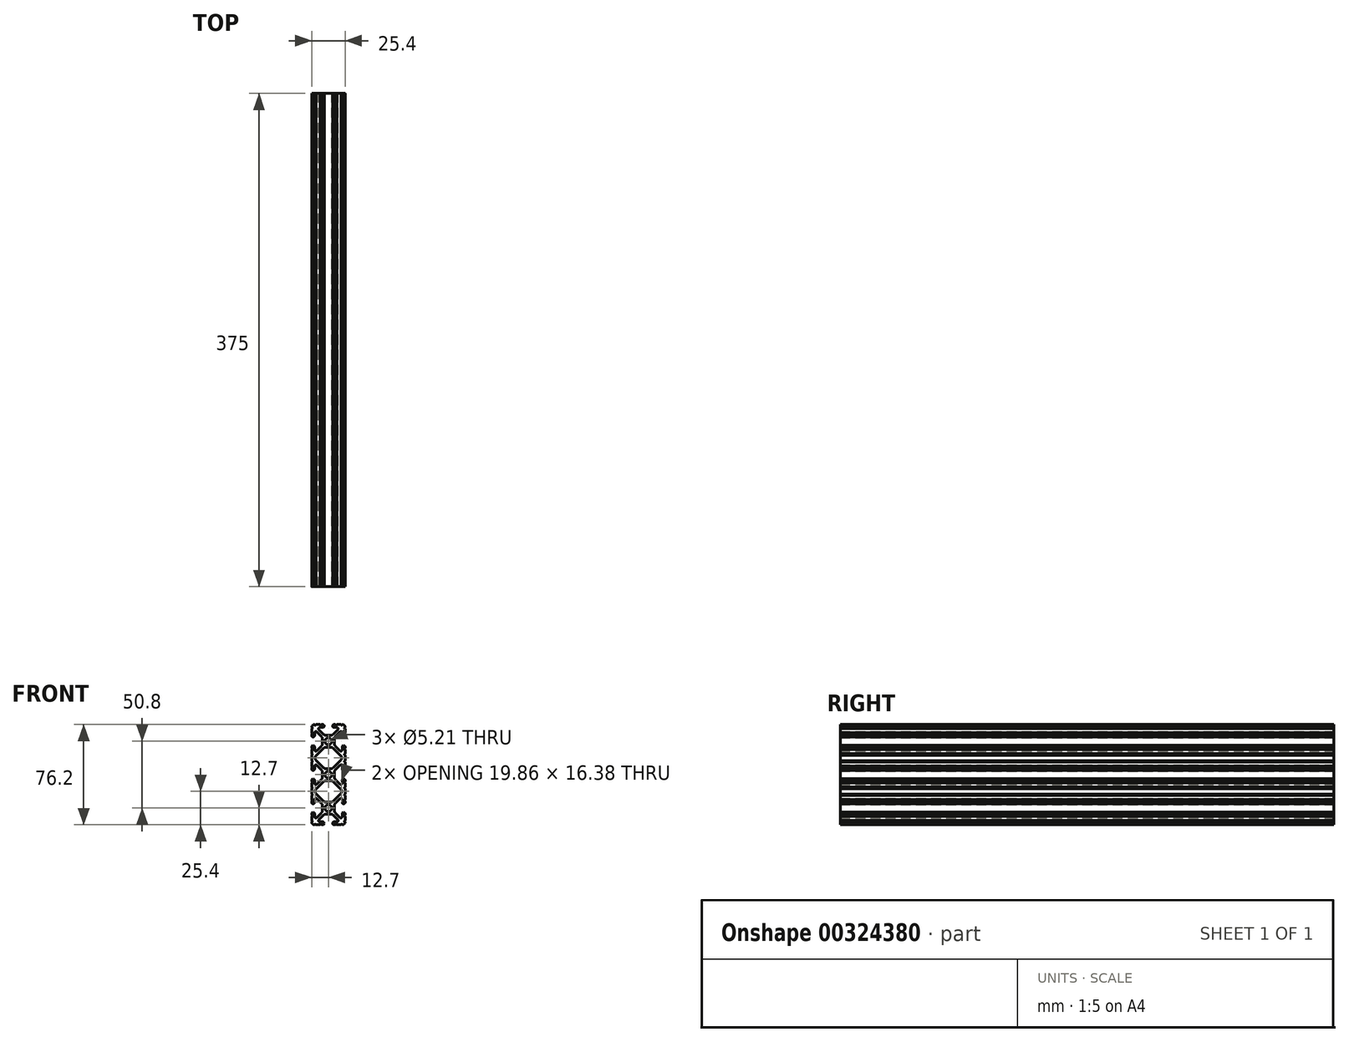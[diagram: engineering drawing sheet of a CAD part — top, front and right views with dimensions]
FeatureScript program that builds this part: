
annotation { "Feature Type Name" : "Feature", "Feature Type Description" : "" }
export const myFeature = defineFeature(function(context is Context, id is Id, definition is map)
    precondition{}
    {
        {
            var Q0;
            Q0=qCreatedBy(makeId("Front.planeOp"),FACE);
            var sketch = newSketch(context, id + "F0", { "sketchPlane" : qUnion([Q0])});
            skArc(sketch, "E0", {"start": v(2.6, 25.4) * mm, "mid": v(0, 28) * mm, "end": v(-2.6, 25.4) * mm});
            skArc(sketch, "E1", {"start": v(-2.6, 25.4) * mm, "mid": v(0, 22.8) * mm, "end": v(2.6, 25.4) * mm});
            skArc(sketch, "E2", {"start": v(-10.57, 38.1) * mm, "mid": v(-10.06, 37.6) * mm, "end": v(-9.55, 38.1) * mm});
            skArc(sketch, "E3", {"start": v(-10.57, 38.1) * mm, "mid": v(-12.08, 37.48) * mm, "end": v(-12.7, 35.97) * mm});
            skArc(sketch, "E4", {"start": v(-12.7, 34.95) * mm, "mid": v(-12.2, 35.46) * mm, "end": v(-12.7, 35.97) * mm});
            skLineSegment(sketch, "E5", {"start": v(-12.7, 34.95) * mm, "end": v(-12.7, 31.72) * mm});
            skArc(sketch, "E6", {"start": v(-12.7, 30.7) * mm, "mid": v(-12.2, 31.22) * mm, "end": v(-12.7, 31.72) * mm});
            skLineSegment(sketch, "E7", {"start": v(-12.7, 30.7) * mm, "end": v(-12.7, 29.7) * mm});
            skArc(sketch, "E8", {"start": v(-12.7, 29.7) * mm, "mid": v(-11.6, 28.6) * mm, "end": v(-10.5, 29.7) * mm});
            skLineSegment(sketch, "E9", {"start": v(-10.5, 29.7) * mm, "end": v(-10.5, 31.87) * mm});
            skArc(sketch, "E10", {"start": v(-8.76, 32.6) * mm, "mid": v(-9.86, 32.81) * mm, "end": v(-10.5, 31.87) * mm});
            skLineSegment(sketch, "E11", {"start": v(-8.76, 32.6) * mm, "end": v(-5.44, 29.28) * mm});
            skArc(sketch, "E12", {"start": v(-4.5, 27.03) * mm, "mid": v(-4.75, 28.25) * mm, "end": v(-5.44, 29.28) * mm});
            skLineSegment(sketch, "E13", {"start": v(-4.5, 27.03) * mm, "end": v(-4.5, 23.77) * mm});
            skArc(sketch, "E14", {"start": v(-5.44, 21.52) * mm, "mid": v(-4.75, 22.55) * mm, "end": v(-4.5, 23.77) * mm});
            skLineSegment(sketch, "E15", {"start": v(-5.44, 21.52) * mm, "end": v(-8.76, 18.2) * mm});
            skArc(sketch, "E16", {"start": v(-10.5, 18.93) * mm, "mid": v(-9.86, 17.99) * mm, "end": v(-8.76, 18.2) * mm});
            skLineSegment(sketch, "E17", {"start": v(-10.5, 18.93) * mm, "end": v(-10.5, 21.1) * mm});
            skArc(sketch, "E18", {"start": v(-10.5, 21.1) * mm, "mid": v(-11.6, 22.2) * mm, "end": v(-12.7, 21.1) * mm});
            skLineSegment(sketch, "E19", {"start": v(-12.7, 21.1) * mm, "end": v(-12.7, 20.1) * mm});
            skArc(sketch, "E20", {"start": v(-12.7, 19.08) * mm, "mid": v(-12.2, 19.58) * mm, "end": v(-12.7, 20.1) * mm});
            skLineSegment(sketch, "E21", {"start": v(-12.7, 19.08) * mm, "end": v(-12.7, 15.85) * mm});
            skArc(sketch, "E22", {"start": v(-12.7, 14.83) * mm, "mid": v(-12.2, 15.34) * mm, "end": v(-12.7, 15.85) * mm});
            skLineSegment(sketch, "E23", {"start": v(-12.7, 14.83) * mm, "end": v(-12.7, 10.57) * mm});
            skArc(sketch, "E24", {"start": v(-12.7, 9.55) * mm, "mid": v(-12.2, 10.06) * mm, "end": v(-12.7, 10.57) * mm});
            skLineSegment(sketch, "E25", {"start": v(-12.7, 9.55) * mm, "end": v(-12.7, 6.32) * mm});
            skArc(sketch, "E26", {"start": v(-12.7, 5.3) * mm, "mid": v(-12.2, 5.82) * mm, "end": v(-12.7, 6.32) * mm});
            skLineSegment(sketch, "E27", {"start": v(-12.7, 5.3) * mm, "end": v(-12.7, 4.3) * mm});
            skArc(sketch, "E28", {"start": v(-12.7, 4.3) * mm, "mid": v(-11.6, 3.2) * mm, "end": v(-10.5, 4.3) * mm});
            skLineSegment(sketch, "E29", {"start": v(-10.5, 4.3) * mm, "end": v(-10.5, 6.47) * mm});
            skArc(sketch, "E30", {"start": v(-8.76, 7.2) * mm, "mid": v(-9.86, 7.41) * mm, "end": v(-10.5, 6.47) * mm});
            skLineSegment(sketch, "E31", {"start": v(-8.76, 7.2) * mm, "end": v(-5.44, 3.88) * mm});
            skArc(sketch, "E32", {"start": v(-4.5, 1.63) * mm, "mid": v(-4.75, 2.85) * mm, "end": v(-5.44, 3.88) * mm});
            skLineSegment(sketch, "E33", {"start": v(-4.5, 1.63) * mm, "end": v(-4.5, -1.63) * mm});
            skArc(sketch, "E34", {"start": v(-5.44, -3.88) * mm, "mid": v(-4.75, -2.85) * mm, "end": v(-4.5, -1.63) * mm});
            skLineSegment(sketch, "E35", {"start": v(-5.44, -3.88) * mm, "end": v(-8.76, -7.2) * mm});
            skArc(sketch, "E36", {"start": v(-10.5, -6.47) * mm, "mid": v(-9.86, -7.41) * mm, "end": v(-8.76, -7.2) * mm});
            skLineSegment(sketch, "E37", {"start": v(-10.5, -6.47) * mm, "end": v(-10.5, -4.3) * mm});
            skArc(sketch, "E38", {"start": v(-10.5, -4.3) * mm, "mid": v(-11.6, -3.2) * mm, "end": v(-12.7, -4.3) * mm});
            skLineSegment(sketch, "E39", {"start": v(-12.7, -4.3) * mm, "end": v(-12.7, -5.3) * mm});
            skArc(sketch, "E40", {"start": v(-12.7, -6.32) * mm, "mid": v(-12.2, -5.82) * mm, "end": v(-12.7, -5.3) * mm});
            skLineSegment(sketch, "E41", {"start": v(-12.7, -6.32) * mm, "end": v(-12.7, -9.55) * mm});
            skArc(sketch, "E42", {"start": v(-12.7, -10.57) * mm, "mid": v(-12.2, -10.06) * mm, "end": v(-12.7, -9.55) * mm});
            skLineSegment(sketch, "E43", {"start": v(-12.7, -10.57) * mm, "end": v(-12.7, -14.83) * mm});
            skArc(sketch, "E44", {"start": v(-12.7, -15.85) * mm, "mid": v(-12.2, -15.34) * mm, "end": v(-12.7, -14.83) * mm});
            skLineSegment(sketch, "E45", {"start": v(-12.7, -15.85) * mm, "end": v(-12.7, -19.08) * mm});
            skArc(sketch, "E46", {"start": v(-12.7, -20.1) * mm, "mid": v(-12.2, -19.58) * mm, "end": v(-12.7, -19.08) * mm});
            skLineSegment(sketch, "E47", {"start": v(-12.7, -20.1) * mm, "end": v(-12.7, -21.1) * mm});
            skArc(sketch, "E48", {"start": v(-12.7, -21.1) * mm, "mid": v(-11.6, -22.2) * mm, "end": v(-10.5, -21.1) * mm});
            skLineSegment(sketch, "E49", {"start": v(-10.5, -21.1) * mm, "end": v(-10.5, -18.93) * mm});
            skArc(sketch, "E50", {"start": v(-8.76, -18.2) * mm, "mid": v(-9.86, -17.99) * mm, "end": v(-10.5, -18.93) * mm});
            skLineSegment(sketch, "E51", {"start": v(-8.76, -18.2) * mm, "end": v(-5.44, -21.52) * mm});
            skArc(sketch, "E52", {"start": v(-4.5, -23.77) * mm, "mid": v(-4.75, -22.55) * mm, "end": v(-5.44, -21.52) * mm});
            skLineSegment(sketch, "E53", {"start": v(-4.5, -23.77) * mm, "end": v(-4.5, -27.03) * mm});
            skArc(sketch, "E54", {"start": v(-5.44, -29.28) * mm, "mid": v(-4.75, -28.25) * mm, "end": v(-4.5, -27.03) * mm});
            skLineSegment(sketch, "E55", {"start": v(-5.44, -29.28) * mm, "end": v(-8.76, -32.6) * mm});
            skArc(sketch, "E56", {"start": v(-10.5, -31.87) * mm, "mid": v(-9.86, -32.81) * mm, "end": v(-8.76, -32.6) * mm});
            skLineSegment(sketch, "E57", {"start": v(-10.5, -31.87) * mm, "end": v(-10.5, -29.7) * mm});
            skArc(sketch, "E58", {"start": v(-10.5, -29.7) * mm, "mid": v(-11.6, -28.6) * mm, "end": v(-12.7, -29.7) * mm});
            skLineSegment(sketch, "E59", {"start": v(-12.7, -29.7) * mm, "end": v(-12.7, -30.7) * mm});
            skArc(sketch, "E60", {"start": v(-12.7, -31.72) * mm, "mid": v(-12.2, -31.22) * mm, "end": v(-12.7, -30.7) * mm});
            skLineSegment(sketch, "E61", {"start": v(-12.7, -31.72) * mm, "end": v(-12.7, -34.95) * mm});
            skArc(sketch, "E62", {"start": v(-12.7, -35.97) * mm, "mid": v(-12.2, -35.46) * mm, "end": v(-12.7, -34.95) * mm});
            skArc(sketch, "E63", {"start": v(-12.7, -35.97) * mm, "mid": v(-12.08, -37.48) * mm, "end": v(-10.57, -38.1) * mm});
            skArc(sketch, "E64", {"start": v(-9.55, -38.1) * mm, "mid": v(-10.06, -37.6) * mm, "end": v(-10.57, -38.1) * mm});
            skLineSegment(sketch, "E65", {"start": v(-9.55, -38.1) * mm, "end": v(-6.32, -38.1) * mm});
            skArc(sketch, "E66", {"start": v(-5.3, -38.1) * mm, "mid": v(-5.82, -37.6) * mm, "end": v(-6.32, -38.1) * mm});
            skLineSegment(sketch, "E67", {"start": v(-5.3, -38.1) * mm, "end": v(-4.3, -38.1) * mm});
            skArc(sketch, "E68", {"start": v(-4.3, -38.1) * mm, "mid": v(-3.2, -37) * mm, "end": v(-4.3, -35.9) * mm});
            skLineSegment(sketch, "E69", {"start": v(-4.3, -35.9) * mm, "end": v(-6.47, -35.9) * mm});
            skArc(sketch, "E70", {"start": v(-7.2, -34.16) * mm, "mid": v(-7.41, -35.26) * mm, "end": v(-6.47, -35.9) * mm});
            skLineSegment(sketch, "E71", {"start": v(-7.2, -34.16) * mm, "end": v(-3.88, -30.84) * mm});
            skArc(sketch, "E72", {"start": v(-1.63, -29.9) * mm, "mid": v(-2.85, -30.15) * mm, "end": v(-3.88, -30.84) * mm});
            skLineSegment(sketch, "E73", {"start": v(-1.63, -29.9) * mm, "end": v(1.63, -29.9) * mm});
            skArc(sketch, "E74", {"start": v(3.88, -30.84) * mm, "mid": v(2.85, -30.15) * mm, "end": v(1.63, -29.9) * mm});
            skLineSegment(sketch, "E75", {"start": v(3.88, -30.84) * mm, "end": v(7.2, -34.16) * mm});
            skArc(sketch, "E76", {"start": v(6.47, -35.9) * mm, "mid": v(7.41, -35.26) * mm, "end": v(7.2, -34.16) * mm});
            skLineSegment(sketch, "E77", {"start": v(6.47, -35.9) * mm, "end": v(4.3, -35.9) * mm});
            skArc(sketch, "E78", {"start": v(4.3, -35.9) * mm, "mid": v(3.2, -37) * mm, "end": v(4.3, -38.1) * mm});
            skLineSegment(sketch, "E79", {"start": v(4.3, -38.1) * mm, "end": v(5.3, -38.1) * mm});
            skArc(sketch, "E80", {"start": v(6.32, -38.1) * mm, "mid": v(5.82, -37.6) * mm, "end": v(5.3, -38.1) * mm});
            skLineSegment(sketch, "E81", {"start": v(6.32, -38.1) * mm, "end": v(9.55, -38.1) * mm});
            skArc(sketch, "E82", {"start": v(10.57, -38.1) * mm, "mid": v(10.06, -37.6) * mm, "end": v(9.55, -38.1) * mm});
            skArc(sketch, "E83", {"start": v(10.57, -38.1) * mm, "mid": v(12.08, -37.48) * mm, "end": v(12.7, -35.97) * mm});
            skArc(sketch, "E84", {"start": v(12.7, -34.95) * mm, "mid": v(12.2, -35.46) * mm, "end": v(12.7, -35.97) * mm});
            skLineSegment(sketch, "E85", {"start": v(12.7, -34.95) * mm, "end": v(12.7, -31.72) * mm});
            skArc(sketch, "E86", {"start": v(12.7, -30.7) * mm, "mid": v(12.2, -31.22) * mm, "end": v(12.7, -31.72) * mm});
            skLineSegment(sketch, "E87", {"start": v(12.7, -30.7) * mm, "end": v(12.7, -29.7) * mm});
            skArc(sketch, "E88", {"start": v(12.7, -29.7) * mm, "mid": v(11.6, -28.6) * mm, "end": v(10.5, -29.7) * mm});
            skLineSegment(sketch, "E89", {"start": v(10.5, -29.7) * mm, "end": v(10.5, -31.87) * mm});
            skArc(sketch, "E90", {"start": v(8.76, -32.6) * mm, "mid": v(9.86, -32.81) * mm, "end": v(10.5, -31.87) * mm});
            skLineSegment(sketch, "E91", {"start": v(8.76, -32.6) * mm, "end": v(5.44, -29.28) * mm});
            skArc(sketch, "E92", {"start": v(4.5, -27.03) * mm, "mid": v(4.75, -28.25) * mm, "end": v(5.44, -29.28) * mm});
            skLineSegment(sketch, "E93", {"start": v(4.5, -27.03) * mm, "end": v(4.5, -23.77) * mm});
            skArc(sketch, "E94", {"start": v(5.44, -21.52) * mm, "mid": v(4.75, -22.55) * mm, "end": v(4.5, -23.77) * mm});
            skLineSegment(sketch, "E95", {"start": v(5.44, -21.52) * mm, "end": v(8.76, -18.2) * mm});
            skArc(sketch, "E96", {"start": v(10.5, -18.93) * mm, "mid": v(9.86, -17.99) * mm, "end": v(8.76, -18.2) * mm});
            skLineSegment(sketch, "E97", {"start": v(10.5, -18.93) * mm, "end": v(10.5, -21.1) * mm});
            skArc(sketch, "E98", {"start": v(10.5, -21.1) * mm, "mid": v(11.6, -22.2) * mm, "end": v(12.7, -21.1) * mm});
            skLineSegment(sketch, "E99", {"start": v(12.7, -21.1) * mm, "end": v(12.7, -20.1) * mm});
            skArc(sketch, "E100", {"start": v(12.7, -19.08) * mm, "mid": v(12.2, -19.58) * mm, "end": v(12.7, -20.1) * mm});
            skLineSegment(sketch, "E101", {"start": v(12.7, -19.08) * mm, "end": v(12.7, -15.85) * mm});
            skArc(sketch, "E102", {"start": v(12.7, -14.83) * mm, "mid": v(12.2, -15.34) * mm, "end": v(12.7, -15.85) * mm});
            skLineSegment(sketch, "E103", {"start": v(12.7, -14.83) * mm, "end": v(12.7, -10.57) * mm});
            skArc(sketch, "E104", {"start": v(12.7, -9.55) * mm, "mid": v(12.2, -10.06) * mm, "end": v(12.7, -10.57) * mm});
            skLineSegment(sketch, "E105", {"start": v(12.7, -9.55) * mm, "end": v(12.7, -6.32) * mm});
            skArc(sketch, "E106", {"start": v(12.7, -5.3) * mm, "mid": v(12.2, -5.82) * mm, "end": v(12.7, -6.32) * mm});
            skLineSegment(sketch, "E107", {"start": v(12.7, -5.3) * mm, "end": v(12.7, -4.3) * mm});
            skArc(sketch, "E108", {"start": v(12.7, -4.3) * mm, "mid": v(11.6, -3.2) * mm, "end": v(10.5, -4.3) * mm});
            skLineSegment(sketch, "E109", {"start": v(10.5, -4.3) * mm, "end": v(10.5, -6.47) * mm});
            skArc(sketch, "E110", {"start": v(8.76, -7.2) * mm, "mid": v(9.86, -7.41) * mm, "end": v(10.5, -6.47) * mm});
            skLineSegment(sketch, "E111", {"start": v(8.76, -7.2) * mm, "end": v(5.44, -3.88) * mm});
            skArc(sketch, "E112", {"start": v(4.5, -1.63) * mm, "mid": v(4.75, -2.85) * mm, "end": v(5.44, -3.88) * mm});
            skLineSegment(sketch, "E113", {"start": v(4.5, -1.63) * mm, "end": v(4.5, 1.63) * mm});
            skArc(sketch, "E114", {"start": v(5.44, 3.88) * mm, "mid": v(4.75, 2.85) * mm, "end": v(4.5, 1.63) * mm});
            skLineSegment(sketch, "E115", {"start": v(5.44, 3.88) * mm, "end": v(8.76, 7.2) * mm});
            skArc(sketch, "E116", {"start": v(10.5, 6.47) * mm, "mid": v(9.86, 7.41) * mm, "end": v(8.76, 7.2) * mm});
            skLineSegment(sketch, "E117", {"start": v(10.5, 6.47) * mm, "end": v(10.5, 4.3) * mm});
            skArc(sketch, "E118", {"start": v(10.5, 4.3) * mm, "mid": v(11.6, 3.2) * mm, "end": v(12.7, 4.3) * mm});
            skLineSegment(sketch, "E119", {"start": v(12.7, 4.3) * mm, "end": v(12.7, 5.3) * mm});
            skArc(sketch, "E120", {"start": v(12.7, 6.32) * mm, "mid": v(12.2, 5.82) * mm, "end": v(12.7, 5.3) * mm});
            skLineSegment(sketch, "E121", {"start": v(12.7, 6.32) * mm, "end": v(12.7, 9.55) * mm});
            skArc(sketch, "E122", {"start": v(12.7, 10.57) * mm, "mid": v(12.2, 10.06) * mm, "end": v(12.7, 9.55) * mm});
            skLineSegment(sketch, "E123", {"start": v(12.7, 10.57) * mm, "end": v(12.7, 14.83) * mm});
            skArc(sketch, "E124", {"start": v(12.7, 15.85) * mm, "mid": v(12.2, 15.34) * mm, "end": v(12.7, 14.83) * mm});
            skLineSegment(sketch, "E125", {"start": v(12.7, 15.85) * mm, "end": v(12.7, 19.08) * mm});
            skArc(sketch, "E126", {"start": v(12.7, 20.1) * mm, "mid": v(12.2, 19.58) * mm, "end": v(12.7, 19.08) * mm});
            skLineSegment(sketch, "E127", {"start": v(12.7, 20.1) * mm, "end": v(12.7, 21.1) * mm});
            skArc(sketch, "E128", {"start": v(12.7, 21.1) * mm, "mid": v(11.6, 22.2) * mm, "end": v(10.5, 21.1) * mm});
            skLineSegment(sketch, "E129", {"start": v(10.5, 21.1) * mm, "end": v(10.5, 18.93) * mm});
            skArc(sketch, "E130", {"start": v(8.76, 18.2) * mm, "mid": v(9.86, 17.99) * mm, "end": v(10.5, 18.93) * mm});
            skLineSegment(sketch, "E131", {"start": v(8.76, 18.2) * mm, "end": v(5.44, 21.52) * mm});
            skArc(sketch, "E132", {"start": v(4.5, 23.77) * mm, "mid": v(4.75, 22.55) * mm, "end": v(5.44, 21.52) * mm});
            skLineSegment(sketch, "E133", {"start": v(4.5, 23.77) * mm, "end": v(4.5, 27.03) * mm});
            skArc(sketch, "E134", {"start": v(5.44, 29.28) * mm, "mid": v(4.75, 28.25) * mm, "end": v(4.5, 27.03) * mm});
            skLineSegment(sketch, "E135", {"start": v(5.44, 29.28) * mm, "end": v(8.76, 32.6) * mm});
            skArc(sketch, "E136", {"start": v(10.5, 31.87) * mm, "mid": v(9.86, 32.81) * mm, "end": v(8.76, 32.6) * mm});
            skLineSegment(sketch, "E137", {"start": v(10.5, 31.87) * mm, "end": v(10.5, 29.7) * mm});
            skArc(sketch, "E138", {"start": v(10.5, 29.7) * mm, "mid": v(11.6, 28.6) * mm, "end": v(12.7, 29.7) * mm});
            skLineSegment(sketch, "E139", {"start": v(12.7, 29.7) * mm, "end": v(12.7, 30.7) * mm});
            skArc(sketch, "E140", {"start": v(12.7, 31.72) * mm, "mid": v(12.2, 31.22) * mm, "end": v(12.7, 30.7) * mm});
            skLineSegment(sketch, "E141", {"start": v(12.7, 31.72) * mm, "end": v(12.7, 34.95) * mm});
            skArc(sketch, "E142", {"start": v(12.7, 35.97) * mm, "mid": v(12.2, 35.46) * mm, "end": v(12.7, 34.95) * mm});
            skArc(sketch, "E143", {"start": v(12.7, 35.97) * mm, "mid": v(12.08, 37.48) * mm, "end": v(10.57, 38.1) * mm});
            skArc(sketch, "E144", {"start": v(9.55, 38.1) * mm, "mid": v(10.06, 37.6) * mm, "end": v(10.57, 38.1) * mm});
            skLineSegment(sketch, "E145", {"start": v(9.55, 38.1) * mm, "end": v(6.32, 38.1) * mm});
            skArc(sketch, "E146", {"start": v(5.3, 38.1) * mm, "mid": v(5.82, 37.6) * mm, "end": v(6.32, 38.1) * mm});
            skLineSegment(sketch, "E147", {"start": v(5.3, 38.1) * mm, "end": v(4.3, 38.1) * mm});
            skArc(sketch, "E148", {"start": v(4.3, 38.1) * mm, "mid": v(3.2, 37) * mm, "end": v(4.3, 35.9) * mm});
            skLineSegment(sketch, "E149", {"start": v(4.3, 35.9) * mm, "end": v(6.47, 35.9) * mm});
            skArc(sketch, "E150", {"start": v(7.2, 34.16) * mm, "mid": v(7.41, 35.26) * mm, "end": v(6.47, 35.9) * mm});
            skLineSegment(sketch, "E151", {"start": v(7.2, 34.16) * mm, "end": v(3.88, 30.84) * mm});
            skArc(sketch, "E152", {"start": v(1.63, 29.9) * mm, "mid": v(2.85, 30.15) * mm, "end": v(3.88, 30.84) * mm});
            skLineSegment(sketch, "E153", {"start": v(1.63, 29.9) * mm, "end": v(-1.63, 29.9) * mm});
            skArc(sketch, "E154", {"start": v(-3.88, 30.84) * mm, "mid": v(-2.85, 30.15) * mm, "end": v(-1.63, 29.9) * mm});
            skLineSegment(sketch, "E155", {"start": v(-3.88, 30.84) * mm, "end": v(-7.2, 34.16) * mm});
            skArc(sketch, "E156", {"start": v(-6.47, 35.9) * mm, "mid": v(-7.41, 35.26) * mm, "end": v(-7.2, 34.16) * mm});
            skLineSegment(sketch, "E157", {"start": v(-6.47, 35.9) * mm, "end": v(-4.3, 35.9) * mm});
            skArc(sketch, "E158", {"start": v(-4.3, 35.9) * mm, "mid": v(-3.2, 37) * mm, "end": v(-4.3, 38.1) * mm});
            skLineSegment(sketch, "E159", {"start": v(-4.3, 38.1) * mm, "end": v(-5.3, 38.1) * mm});
            skArc(sketch, "E160", {"start": v(-6.32, 38.1) * mm, "mid": v(-5.82, 37.6) * mm, "end": v(-5.3, 38.1) * mm});
            skLineSegment(sketch, "E161", {"start": v(-6.32, 38.1) * mm, "end": v(-9.55, 38.1) * mm});
            skArc(sketch, "E162", {"start": v(2.6, 0) * mm, "mid": v(0, 2.6) * mm, "end": v(-2.6, 0) * mm});
            skArc(sketch, "E163", {"start": v(-2.6, 0) * mm, "mid": v(0, -2.6) * mm, "end": v(2.6, 0) * mm});
            skArc(sketch, "E164", {"start": v(2.6, -25.4) * mm, "mid": v(0, -22.8) * mm, "end": v(-2.6, -25.4) * mm});
            skArc(sketch, "E165", {"start": v(-2.6, -25.4) * mm, "mid": v(0, -28) * mm, "end": v(2.6, -25.4) * mm});
            skLineSegment(sketch, "E166", {"start": v(-3.88, -5.44) * mm, "end": v(-9.47, -11.03) * mm});
            skArc(sketch, "E167", {"start": v(-1.63, -4.5) * mm, "mid": v(-2.85, -4.75) * mm, "end": v(-3.88, -5.44) * mm});
            skLineSegment(sketch, "E168", {"start": v(1.63, -4.5) * mm, "end": v(-1.63, -4.5) * mm});
            skArc(sketch, "E169", {"start": v(3.88, -5.44) * mm, "mid": v(2.85, -4.75) * mm, "end": v(1.63, -4.5) * mm});
            skLineSegment(sketch, "E170", {"start": v(9.47, -11.03) * mm, "end": v(3.88, -5.44) * mm});
            skArc(sketch, "E171", {"start": v(9.93, -12.15) * mm, "mid": v(9.81, -11.54) * mm, "end": v(9.47, -11.03) * mm});
            skLineSegment(sketch, "E172", {"start": v(9.93, -13.25) * mm, "end": v(9.93, -12.15) * mm});
            skArc(sketch, "E173", {"start": v(9.47, -14.37) * mm, "mid": v(9.81, -13.86) * mm, "end": v(9.93, -13.25) * mm});
            skLineSegment(sketch, "E174", {"start": v(3.88, -19.96) * mm, "end": v(9.47, -14.37) * mm});
            skArc(sketch, "E175", {"start": v(1.63, -20.9) * mm, "mid": v(2.85, -20.65) * mm, "end": v(3.88, -19.96) * mm});
            skLineSegment(sketch, "E176", {"start": v(-1.63, -20.9) * mm, "end": v(1.63, -20.9) * mm});
            skArc(sketch, "E177", {"start": v(-3.88, -19.96) * mm, "mid": v(-2.85, -20.65) * mm, "end": v(-1.63, -20.9) * mm});
            skLineSegment(sketch, "E178", {"start": v(-9.47, -14.37) * mm, "end": v(-3.88, -19.96) * mm});
            skArc(sketch, "E179", {"start": v(-9.93, -13.25) * mm, "mid": v(-9.81, -13.86) * mm, "end": v(-9.47, -14.37) * mm});
            skLineSegment(sketch, "E180", {"start": v(-9.93, -12.15) * mm, "end": v(-9.93, -13.25) * mm});
            skArc(sketch, "E181", {"start": v(-9.47, -11.03) * mm, "mid": v(-9.81, -11.54) * mm, "end": v(-9.93, -12.15) * mm});
            skLineSegment(sketch, "E182", {"start": v(-3.88, 19.96) * mm, "end": v(-9.47, 14.37) * mm});
            skArc(sketch, "E183", {"start": v(-1.63, 20.9) * mm, "mid": v(-2.85, 20.65) * mm, "end": v(-3.88, 19.96) * mm});
            skLineSegment(sketch, "E184", {"start": v(1.63, 20.9) * mm, "end": v(-1.63, 20.9) * mm});
            skArc(sketch, "E185", {"start": v(3.88, 19.96) * mm, "mid": v(2.85, 20.65) * mm, "end": v(1.63, 20.9) * mm});
            skLineSegment(sketch, "E186", {"start": v(9.47, 14.37) * mm, "end": v(3.88, 19.96) * mm});
            skArc(sketch, "E187", {"start": v(9.93, 13.25) * mm, "mid": v(9.81, 13.86) * mm, "end": v(9.47, 14.37) * mm});
            skLineSegment(sketch, "E188", {"start": v(9.93, 12.15) * mm, "end": v(9.93, 13.25) * mm});
            skArc(sketch, "E189", {"start": v(9.47, 11.03) * mm, "mid": v(9.81, 11.54) * mm, "end": v(9.93, 12.15) * mm});
            skLineSegment(sketch, "E190", {"start": v(3.88, 5.44) * mm, "end": v(9.47, 11.03) * mm});
            skArc(sketch, "E191", {"start": v(1.63, 4.5) * mm, "mid": v(2.85, 4.75) * mm, "end": v(3.88, 5.44) * mm});
            skLineSegment(sketch, "E192", {"start": v(-1.63, 4.5) * mm, "end": v(1.63, 4.5) * mm});
            skArc(sketch, "E193", {"start": v(-3.88, 5.44) * mm, "mid": v(-2.85, 4.75) * mm, "end": v(-1.63, 4.5) * mm});
            skLineSegment(sketch, "E194", {"start": v(-9.47, 11.03) * mm, "end": v(-3.88, 5.44) * mm});
            skArc(sketch, "E195", {"start": v(-9.93, 12.15) * mm, "mid": v(-9.81, 11.54) * mm, "end": v(-9.47, 11.03) * mm});
            skLineSegment(sketch, "E196", {"start": v(-9.93, 13.25) * mm, "end": v(-9.93, 12.15) * mm});
            skArc(sketch, "E197", {"start": v(-9.47, 14.37) * mm, "mid": v(-9.81, 13.86) * mm, "end": v(-9.93, 13.25) * mm});
            skSolve(sketch);
        }
        {
            var Q0;
            Q0=makeQuery(id+"F0.imprint","IMPRINT",FACE,{"disambiguationData":[TD([[makeQuery(id+"F0.imprint","IMPRINT",EDGE,{"derivedFrom":sQuery(id+"F0.wireOp",EDGE,"E0")}),-1.0]])]});
            extrude(context, id + "F1", {"entities" : qUnion([Q0]), "depth" : 375 * mm});
        }
    });
